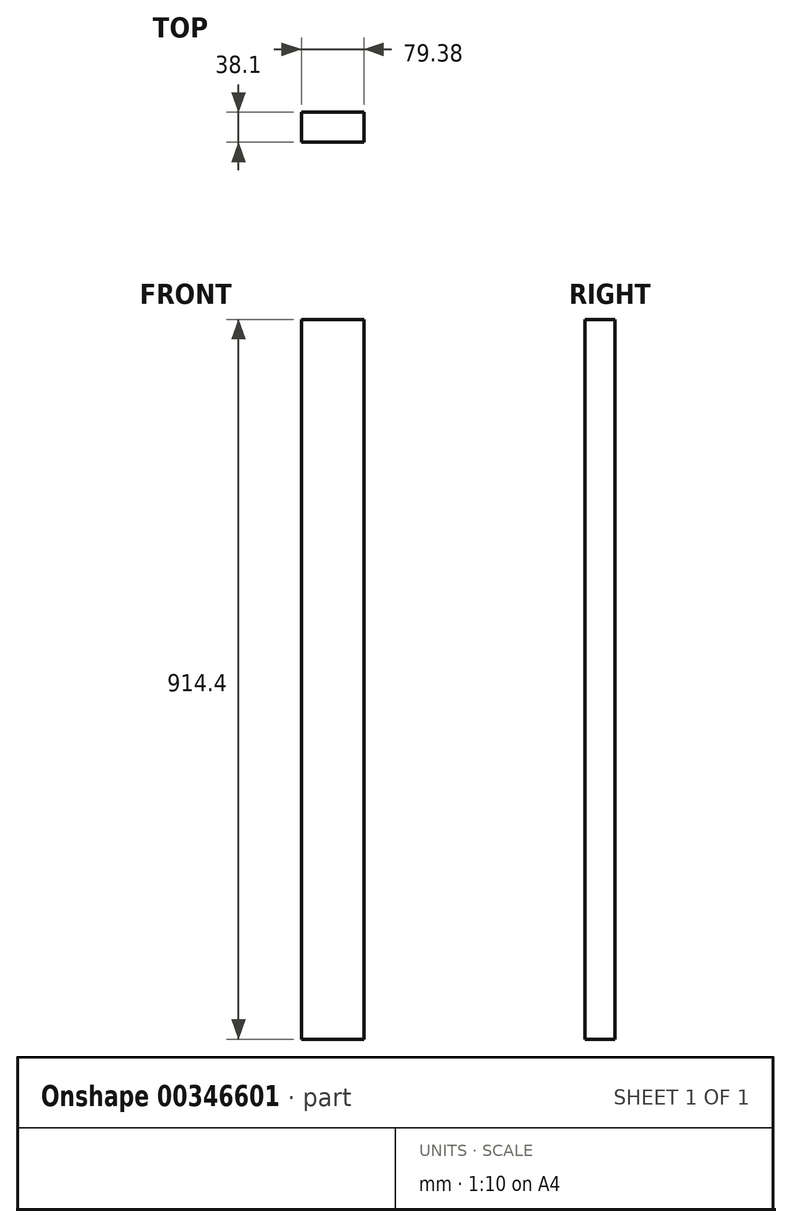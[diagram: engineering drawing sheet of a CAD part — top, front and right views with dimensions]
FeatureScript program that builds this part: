
annotation { "Feature Type Name" : "Feature", "Feature Type Description" : "" }
export const myFeature = defineFeature(function(context is Context, id is Id, definition is map)
    precondition{}
    {
        {
            var Q0;
            Q0=qCreatedBy(makeId("Top.planeOp"),FACE);
            var sketch = newSketch(context, id + "F0", { "sketchPlane" : qUnion([Q0])});
            skLineSegment(sketch, "E0.bottom", {"start": v(39.69, -19.05) * mm, "end": v(-39.69, -19.05) * mm});
            skLineSegment(sketch, "E0.top", {"start": v(39.69, 19.05) * mm, "end": v(-39.69, 19.05) * mm});
            skLineSegment(sketch, "E0.left", {"start": v(39.69, -19.05) * mm, "end": v(39.69, 19.05) * mm});
            skLineSegment(sketch, "E0.right", {"start": v(-39.69, -19.05) * mm, "end": v(-39.69, 19.05) * mm});
            skPoint(sketch, "E0.middle", {"position": v(0, 0) * mm});
            skSolve(sketch);
        }
        {
            var Q0;
            Q0=makeQuery(id+"F0.imprint","IMPRINT",FACE,{"disambiguationData":[TD([[makeQuery(id+"F0.imprint","IMPRINT",EDGE,{"derivedFrom":sQuery(id+"F0.wireOp",EDGE,"E0.bottom")}),-1.0]])]});
            extrude(context, id + "F1", {"entities" : qUnion([Q0]), "depth" : 914.4 * mm});
        }
    });
